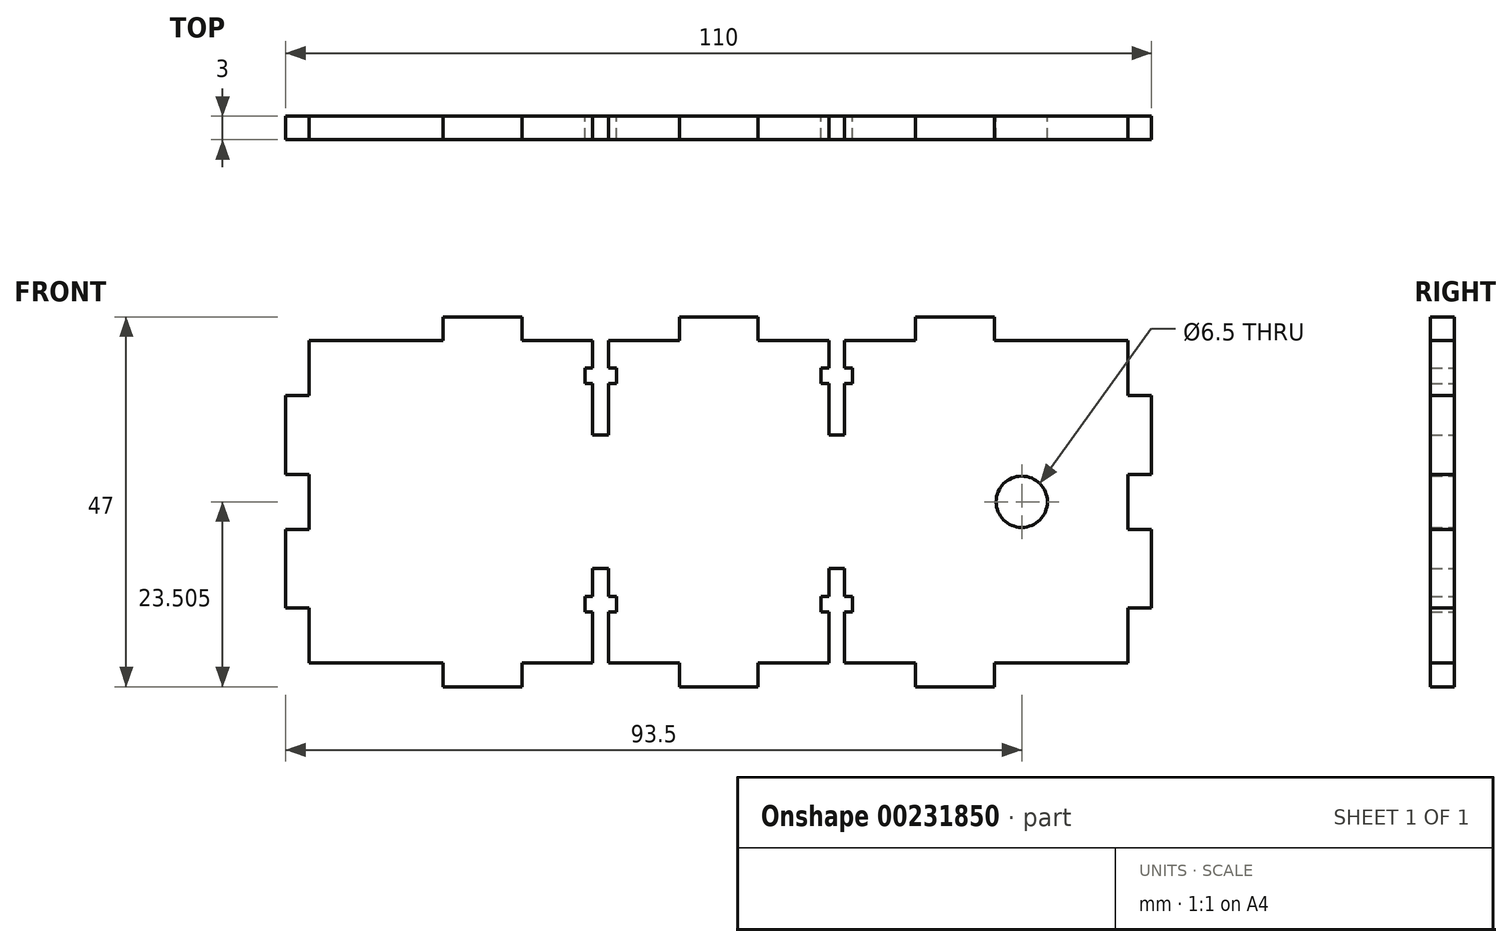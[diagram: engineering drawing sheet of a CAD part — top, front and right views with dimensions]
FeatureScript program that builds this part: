
annotation { "Feature Type Name" : "Feature", "Feature Type Description" : "" }
export const myFeature = defineFeature(function(context is Context, id is Id, definition is map)
    precondition{}
    {
        {
            var Q0;
            Q0=qCreatedBy(makeId("Front.planeOp"),FACE);
            var sketch = newSketch(context, id + "F0", { "sketchPlane" : qUnion([Q0])});
            skLineSegment(sketch, "E0.MirrorCS", {"start": v(-8, 1.38) * mm, "end": v(-8, -1.62) * mm});
            skLineSegment(sketch, "E1.MirrorCS", {"start": v(-38, 1.38) * mm, "end": v(-38, -1.62) * mm});
            skLineSegment(sketch, "E2.MirrorCS", {"start": v(-28, -1.62) * mm, "end": v(-28, 1.38) * mm});
            skLineSegment(sketch, "E3.MirrorCS", {"start": v(-28, 1.38) * mm, "end": v(-19, 1.38) * mm});
            skLineSegment(sketch, "E4.MirrorCS", {"start": v(-55, 1.38) * mm, "end": v(-38, 1.38) * mm});
            skLineSegment(sketch, "E5.MirrorCS", {"start": v(-38, -1.62) * mm, "end": v(-28, -1.62) * mm});
            skLineSegment(sketch, "E6", {"start": v(-55, 1.38) * mm, "end": v(-55, 8.38) * mm});
            skLineSegment(sketch, "E7", {"start": v(-55, 8.38) * mm, "end": v(-58, 8.38) * mm});
            skLineSegment(sketch, "E8", {"start": v(-58, 8.38) * mm, "end": v(-58, 18.38) * mm});
            skLineSegment(sketch, "E9", {"start": v(-58, 18.38) * mm, "end": v(-55, 18.38) * mm});
            skLineSegment(sketch, "E10", {"start": v(-55, 18.38) * mm, "end": v(-55, 25.38) * mm});
            skLineSegment(sketch, "E11", {"start": v(-55, 25.38) * mm, "end": v(-58, 25.38) * mm});
            skLineSegment(sketch, "E12", {"start": v(-58, 25.38) * mm, "end": v(-58, 35.38) * mm});
            skLineSegment(sketch, "E13", {"start": v(-58, 35.38) * mm, "end": v(-55, 35.38) * mm});
            skLineSegment(sketch, "E14", {"start": v(-55, 35.38) * mm, "end": v(-55, 42.38) * mm});
            skLineSegment(sketch, "E15.MirrorCS", {"start": v(-8, 42.38) * mm, "end": v(-8, 45.38) * mm});
            skLineSegment(sketch, "E16.MirrorCS", {"start": v(-38, 42.38) * mm, "end": v(-38, 45.38) * mm});
            skLineSegment(sketch, "E17.MirrorCS", {"start": v(-28, 45.38) * mm, "end": v(-28, 42.38) * mm});
            skLineSegment(sketch, "E18.MirrorCS", {"start": v(-38, 45.38) * mm, "end": v(-28, 45.38) * mm});
            skLineSegment(sketch, "E19.MirrorCS", {"start": v(-55, 42.38) * mm, "end": v(-38, 42.38) * mm});
            skLineSegment(sketch, "E20.MirrorCS", {"start": v(-28, 42.38) * mm, "end": v(-19, 42.38) * mm});
            skLineSegment(sketch, "E21.bottom", {"start": v(-19, 13.38) * mm, "end": v(-17, 13.38) * mm});
            skLineSegment(sketch, "E21.left", {"start": v(-19, 13.38) * mm, "end": v(-19, 9.88) * mm});
            skLineSegment(sketch, "E21.right", {"start": v(-17, 13.38) * mm, "end": v(-17, 9.88) * mm});
            skLineSegment(sketch, "E22.bottom", {"start": v(-20, 9.88) * mm, "end": v(-19, 9.88) * mm});
            skLineSegment(sketch, "E22.top", {"start": v(-20, 7.88) * mm, "end": v(-19, 7.88) * mm});
            skLineSegment(sketch, "E22.left", {"start": v(-20, 9.88) * mm, "end": v(-20, 7.88) * mm});
            skLineSegment(sketch, "E22.right", {"start": v(-16, 9.88) * mm, "end": v(-16, 7.88) * mm});
            skLineSegment(sketch, "E23.trimOffspring", {"start": v(-17, 1.38) * mm, "end": v(-8, 1.38) * mm});
            skLineSegment(sketch, "E24.trimOffspring", {"start": v(-17, 7.88) * mm, "end": v(-16, 7.88) * mm});
            skLineSegment(sketch, "E25.trimOffspring", {"start": v(-17, 7.88) * mm, "end": v(-17, 1.38) * mm});
            skLineSegment(sketch, "E26.trimOffspring", {"start": v(-19, 7.88) * mm, "end": v(-19, 1.38) * mm});
            skLineSegment(sketch, "E27.trimOffspring", {"start": v(-17, 9.88) * mm, "end": v(-16, 9.88) * mm});
            skLineSegment(sketch, "E28.MirrorCS", {"start": v(-19, 38.88) * mm, "end": v(-19, 42.38) * mm});
            skLineSegment(sketch, "E29.MirrorCS", {"start": v(-19, 30.38) * mm, "end": v(-17, 30.38) * mm});
            skLineSegment(sketch, "E30.MirrorCS", {"start": v(-17, 35.88) * mm, "end": v(-17, 36.88) * mm});
            skLineSegment(sketch, "E31.MirrorCS", {"start": v(-20, 36.88) * mm, "end": v(-19, 36.88) * mm});
            skLineSegment(sketch, "E32.MirrorCS", {"start": v(-20, 38.88) * mm, "end": v(-19, 38.88) * mm});
            skLineSegment(sketch, "E33.MirrorCS", {"start": v(-19, 30.38) * mm, "end": v(-19, 36.88) * mm});
            skLineSegment(sketch, "E34.MirrorCS", {"start": v(-20, 36.88) * mm, "end": v(-20, 38.88) * mm});
            skLineSegment(sketch, "E35.MirrorCS", {"start": v(-17, 30.38) * mm, "end": v(-17, 36.88) * mm});
            skLineSegment(sketch, "E36.trimOffspring", {"start": v(-17, 42.38) * mm, "end": v(-8, 42.38) * mm});
            skPoint(sketch, "E37.orphan", {"position": v(0, 69.16) * mm});
            skPoint(sketch, "E38.endSnap0", {"position": v(-56.5, 8.38) * mm});
            skLineSegment(sketch, "E39", {"start": v(-8, 45.38) * mm, "end": v(2, 45.38) * mm});
            skLineSegment(sketch, "E40", {"start": v(2, 45.38) * mm, "end": v(2, 42.38) * mm});
            skLineSegment(sketch, "E41", {"start": v(2, 42.38) * mm, "end": v(11, 42.38) * mm});
            skLineSegment(sketch, "E42", {"start": v(-8, -1.62) * mm, "end": v(2, -1.62) * mm});
            skLineSegment(sketch, "E43", {"start": v(2, -1.62) * mm, "end": v(2, 1.38) * mm});
            skLineSegment(sketch, "E44", {"start": v(2, 1.38) * mm, "end": v(11, 1.38) * mm});
            skLineSegment(sketch, "E45", {"start": v(22, 42.38) * mm, "end": v(22, 45.38) * mm});
            skLineSegment(sketch, "E46", {"start": v(22, 45.38) * mm, "end": v(32, 45.38) * mm});
            skLineSegment(sketch, "E47", {"start": v(32, 45.38) * mm, "end": v(32, 42.38) * mm});
            skLineSegment(sketch, "E48", {"start": v(32, 42.38) * mm, "end": v(49, 42.38) * mm});
            skLineSegment(sketch, "E49", {"start": v(22, 1.38) * mm, "end": v(22, -1.62) * mm});
            skLineSegment(sketch, "E50", {"start": v(22, -1.62) * mm, "end": v(32, -1.62) * mm});
            skLineSegment(sketch, "E51", {"start": v(32, -1.62) * mm, "end": v(32, 1.38) * mm});
            skLineSegment(sketch, "E52", {"start": v(32, 1.38) * mm, "end": v(49, 1.38) * mm});
            skLineSegment(sketch, "E53", {"start": v(49, 42.38) * mm, "end": v(49, 35.38) * mm});
            skLineSegment(sketch, "E54", {"start": v(49, 35.38) * mm, "end": v(52, 35.38) * mm});
            skLineSegment(sketch, "E55", {"start": v(52, 35.38) * mm, "end": v(52, 25.38) * mm});
            skLineSegment(sketch, "E56", {"start": v(52, 25.38) * mm, "end": v(49, 25.38) * mm});
            skLineSegment(sketch, "E57", {"start": v(49, 25.38) * mm, "end": v(49, 18.38) * mm});
            skLineSegment(sketch, "E58", {"start": v(49, 18.38) * mm, "end": v(52, 18.38) * mm});
            skLineSegment(sketch, "E59", {"start": v(52, 18.38) * mm, "end": v(52, 8.38) * mm});
            skLineSegment(sketch, "E60", {"start": v(52, 8.38) * mm, "end": v(49, 8.38) * mm});
            skLineSegment(sketch, "E61", {"start": v(49, 8.38) * mm, "end": v(49, 1.38) * mm});
            skLineSegment(sketch, "E62", {"start": v(-3, 61.79) * mm, "end": v(-3, -7.76) * mm, "construction": true});
            skLineSegment(sketch, "E63.MirrorCS", {"start": v(14, 7.88) * mm, "end": v(13, 7.88) * mm});
            skLineSegment(sketch, "E64.MirrorCS", {"start": v(14, 38.88) * mm, "end": v(13, 38.88) * mm});
            skLineSegment(sketch, "E65.MirrorCS", {"start": v(11, 7.88) * mm, "end": v(10, 7.88) * mm});
            skLineSegment(sketch, "E66.MirrorCS", {"start": v(10, 9.88) * mm, "end": v(10, 7.88) * mm});
            skLineSegment(sketch, "E67.MirrorCS", {"start": v(11, 9.88) * mm, "end": v(10, 9.88) * mm});
            skLineSegment(sketch, "E68.MirrorCS", {"start": v(14, 9.88) * mm, "end": v(14, 7.88) * mm});
            skLineSegment(sketch, "E69.MirrorCS", {"start": v(14, 36.88) * mm, "end": v(14, 38.88) * mm});
            skLineSegment(sketch, "E70.MirrorCS", {"start": v(14, 9.88) * mm, "end": v(13, 9.88) * mm});
            skLineSegment(sketch, "E71.MirrorCS", {"start": v(14, 36.88) * mm, "end": v(13, 36.88) * mm});
            skLineSegment(sketch, "E72.MirrorCS", {"start": v(13, 13.38) * mm, "end": v(11, 13.38) * mm});
            skLineSegment(sketch, "E73.MirrorCS", {"start": v(13, 30.38) * mm, "end": v(11, 30.38) * mm});
            skLineSegment(sketch, "E74.MirrorCS", {"start": v(13, 13.38) * mm, "end": v(13, 9.88) * mm});
            skLineSegment(sketch, "E75.MirrorCS", {"start": v(11, 13.38) * mm, "end": v(11, 9.88) * mm});
            skLineSegment(sketch, "E76.MirrorCS", {"start": v(13, 7.88) * mm, "end": v(13, 1.38) * mm});
            skLineSegment(sketch, "E77.MirrorCS", {"start": v(11, 7.88) * mm, "end": v(11, 1.38) * mm});
            skLineSegment(sketch, "E78.MirrorCS", {"start": v(11, 35.88) * mm, "end": v(11, 36.88) * mm});
            skLineSegment(sketch, "E79.MirrorCS", {"start": v(13, 30.38) * mm, "end": v(13, 36.88) * mm});
            skLineSegment(sketch, "E80.MirrorCS", {"start": v(11, 30.38) * mm, "end": v(11, 36.88) * mm});
            skLineSegment(sketch, "E81.MirrorCS", {"start": v(13, 38.88) * mm, "end": v(13, 42.38) * mm});
            skLineSegment(sketch, "E82.trimOffspring", {"start": v(13, 42.38) * mm, "end": v(22, 42.38) * mm});
            skLineSegment(sketch, "E83.trimOffspring", {"start": v(13, 1.38) * mm, "end": v(22, 1.38) * mm});
            skLineSegment(sketch, "E84", {"start": v(-18, 30.38) * mm, "end": v(-18, 40.74) * mm, "construction": true});
            skLineSegment(sketch, "E85.MirrorCS", {"start": v(-16, 38.88) * mm, "end": v(-17, 38.88) * mm});
            skLineSegment(sketch, "E86.MirrorCS", {"start": v(-16, 36.88) * mm, "end": v(-16, 38.88) * mm});
            skLineSegment(sketch, "E87.MirrorCS", {"start": v(-16, 36.88) * mm, "end": v(-17, 36.88) * mm});
            skLineSegment(sketch, "E88.trimOffspring", {"start": v(-17, 38.88) * mm, "end": v(-17, 42.38) * mm});
            skLineSegment(sketch, "E89", {"start": v(12, 30.38) * mm, "end": v(12, 38.73) * mm, "construction": true});
            skLineSegment(sketch, "E90.MirrorCS", {"start": v(10, 38.88) * mm, "end": v(11, 38.88) * mm});
            skLineSegment(sketch, "E91.MirrorCS", {"start": v(10, 36.88) * mm, "end": v(10, 38.88) * mm});
            skLineSegment(sketch, "E92.MirrorCS", {"start": v(10, 36.88) * mm, "end": v(11, 36.88) * mm});
            skLineSegment(sketch, "E93.trimOffspring", {"start": v(11, 38.88) * mm, "end": v(11, 42.38) * mm});
            skLineSegment(sketch, "E94", {"start": v(49, 42.38) * mm, "end": v(22, 1.38) * mm, "construction": true});
            skLineSegment(sketch, "E95", {"start": v(22, 42.38) * mm, "end": v(49, 1.38) * mm, "construction": true});
            skCircle(sketch, "E96", {"center": v(35.5, 21.88) * mm, "radius": 3.25 * mm});
            skSolve(sketch);
        }
        {
            var Q0;
            Q0=qSketchRegion(id+"F0",true);
            extrude(context, id + "F1", {"entities" : qUnion([Q0]), "endBound" : BoundingType.SYMMETRIC, "depth" : 3 * mm});
        }
    });
